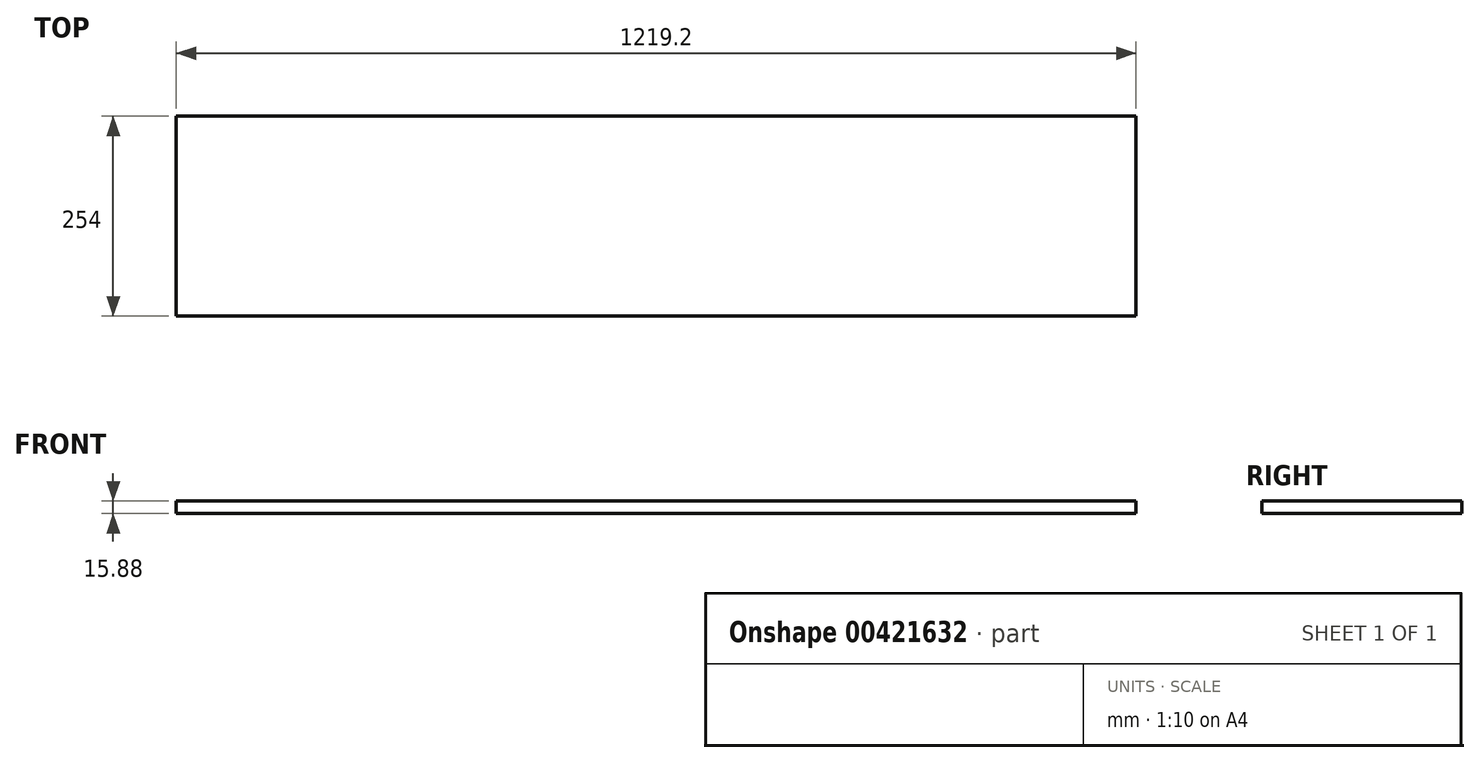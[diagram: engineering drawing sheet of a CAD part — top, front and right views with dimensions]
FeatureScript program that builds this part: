
annotation { "Feature Type Name" : "Feature", "Feature Type Description" : "" }
export const myFeature = defineFeature(function(context is Context, id is Id, definition is map)
    precondition{}
    {
        {
            var Q0;
            Q0=qCreatedBy(makeId("Front.planeOp"),FACE);
            var sketch = newSketch(context, id + "F0", { "sketchPlane" : qUnion([Q0])});
            skLineSegment(sketch, "E0.bottom", {"start": v(0, 0) * mm, "end": v(1219.2, 0) * mm});
            skLineSegment(sketch, "E0.top", {"start": v(0, 15.88) * mm, "end": v(1219.2, 15.88) * mm});
            skLineSegment(sketch, "E0.left", {"start": v(0, 0) * mm, "end": v(0, 15.88) * mm});
            skLineSegment(sketch, "E0.right", {"start": v(1219.2, 0) * mm, "end": v(1219.2, 15.88) * mm});
            skSolve(sketch);
        }
        {
            var Q0;
            Q0=makeQuery(id+"F0.imprint","IMPRINT",FACE,{"disambiguationData":[TD([[makeQuery(id+"F0.imprint","IMPRINT",EDGE,{"derivedFrom":sQuery(id+"F0.wireOp",EDGE,"E0.bottom")}),1.0]])]});
            extrude(context, id + "F1", {"entities" : qUnion([Q0]), "depth" : 254 * mm});
        }
    });
